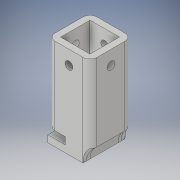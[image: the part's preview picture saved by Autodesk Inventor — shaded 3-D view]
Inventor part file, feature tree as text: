
AUTODESK INVENTOR PART (.ipt)
format: ipt  version: 2019.4 (Build 234330000, 330)  size: 225,792 bytes
history: native  units: mm
features: extrude x8, sketch x8, fillet x3
ambient origin geometry x8: Origin, YZ Plane, XZ Plane, XY Plane, X Axis, Y Axis, Z Axis, Center Point
bodies: Solid1 (feature_tree)
feature tree (19):
  extrude  "Extrusion1"  Depth=30.0mm
  extrude  "Extrusion2"  Depth=4.5mm
  extrude  "Extrusion3"  Depth=21.0mm
  fillet  "Fillet2"  Radius=21.0mm
  extrude  "Extrusion4"  Depth=30.0mm
  fillet  "Fillet3"  Radius=4.0mm
  extrude  "Extrusion5"  Depth=10.0mm
  fillet  "Fillet4"  Radius=10.0mm
  extrude  "Extrusion6"  TaperAngle=0.0deg  [1 undecoded]
  extrude  "Extrusion7"  Depth=5.0mm TaperAngle=0.0deg
  extrude  "Extrusion8"  Depth=30.0mm
  sketch  "Sketch1"  dims[d0=30.0mm d1=30.0mm]
  sketch  "Sketch2"  dims[d2=55.4mm d3=0.0mm d4=4.5mm]
  sketch  "Sketch3"  dims[d5=4.5mm d6=21.0mm d7=21.0mm]
  sketch  "Sketch4"  dims[d8=30.0mm d9=0.0mm d10=15.0mm d11=4.0mm]
  sketch  "Sketch5"  dims[d12=5.0mm d13=0.0mm d15=5.0mm d16=10.0mm]
  sketch  "Sketch6"  dims[d17=6.0mm d18=0.0mm]
  sketch  "Sketch7"  dims[d19=120.0deg d20=5.0mm d21=0.0mm]
  sketch  "Sketch8"  dims[d22=5.0mm d23=25.0mm d24=30.0mm d25=5.0mm d26=0.0mm d27=13.0mm d29=4.0mm d30=5.0mm d31=0.0mm d32=10.0mm d33=5.5mm d34=30.0mm d35=0.0mm d36=10.0mm d37=90.0deg d38=5.5mm d39=30.0mm d40=0.0mm]
note: 1 required parameter value undecoded (feature->parameter linkage not recoverable at this tier; creation-order binding heuristic only, values carry confidence <= 0.55)
